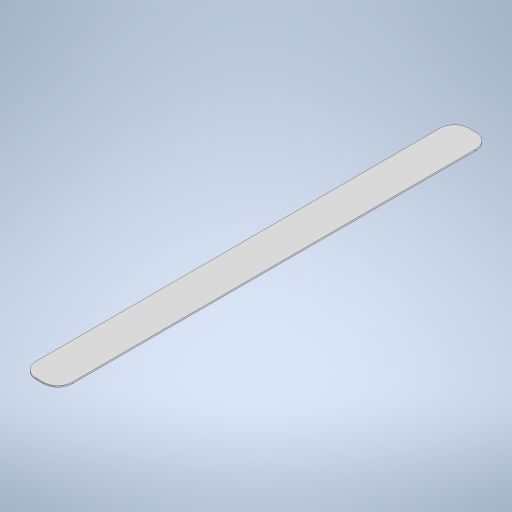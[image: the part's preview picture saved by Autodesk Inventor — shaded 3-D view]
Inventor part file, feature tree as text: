
AUTODESK INVENTOR PART (.ipt)
format: ipt  version: 2023 (Build 270158000, 158)  size: 237,568 bytes
history: native  units: in
note: dims shown in document units (in); Inventor stores cm internally (conversion verified against a paired STEP export)
features: extrude x1, sketch x1
ambient origin geometry x8: Origin, YZ Plane, XZ Plane, XY Plane, X Axis, Y Axis, Z Axis, Center Point
bodies: Solid1 (feature_tree)
feature tree (2):
  extrude  "Extrusion1"  Depth=11.811in
  sketch  "Sketch1"  dims[d0=0.9843in d1=11.811in d2=0.0787in d3=0.3937in d4=0.0394in d5=0.0in]
